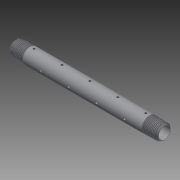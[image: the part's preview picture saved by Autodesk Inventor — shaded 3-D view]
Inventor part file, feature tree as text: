
AUTODESK INVENTOR PART (.ipt)
format: ipt  version: 2014 (Build 180170000, 170)  size: 3,021,312 bytes
history: native  units: in
note: dims shown in document units (in); Inventor stores cm internally (conversion verified against a paired STEP export)
features: other x2, extrude x2, sketch x2, imported_body x1
ambient origin geometry x8: Origin, YZ Plane, XZ Plane, XY Plane, X Axis, Y Axis, Z Axis, Center Point
bodies: Body1 (feature_tree)
feature tree (7):
  parser-record x1  (decoder bookkeeping rows leaked as tree rows — omitted from the tree; the rows remain in map.json)
  other  "4830K179_STD-WALL TYPE 304-304L SS THRD PIPE NIPPLE1"
  extrude  "Extrusion1"  Depth=0.125in
  extrude  "Extrusion2"  Depth=0.75in
  imported_body  "Base1"
  sketch  "Sketch1"  dims[d0=0.125in d1=0.125in]
  sketch  "Sketch2"  dims[d2=0.125in d3=1.5in d4=1.5in d5=1.0in d6=0.0in d7=0.125in d8=0.75in d9=0.125in d10=1.5in d11=1.0in d12=0.0in]
